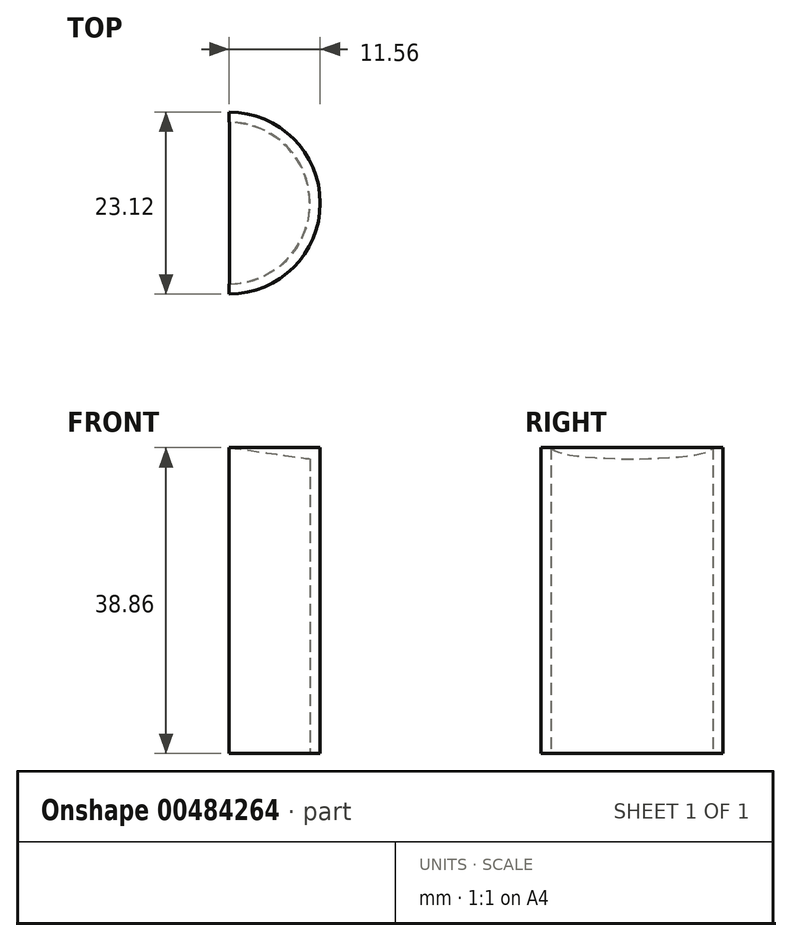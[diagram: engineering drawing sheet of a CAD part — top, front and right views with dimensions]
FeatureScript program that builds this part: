
annotation { "Feature Type Name" : "Feature", "Feature Type Description" : "" }
export const myFeature = defineFeature(function(context is Context, id is Id, definition is map)
    precondition{}
    {
        {
            var Q0;
            Q0=qCreatedBy(makeId("Top.planeOp"),FACE);
            var sketch = newSketch(context, id + "F0", { "sketchPlane" : qUnion([Q0])});
            skArc(sketch, "E0", {"start": v(0, -10.29) * mm, "mid": v(10.29, 0) * mm, "end": v(0, 10.29) * mm});
            skArc(sketch, "E1", {"start": v(0, -11.56) * mm, "mid": v(11.56, 0) * mm, "end": v(0, 11.56) * mm});
            skLineSegment(sketch, "E2", {"start": v(0, 11.56) * mm, "end": v(0, 10.29) * mm});
            skLineSegment(sketch, "E3.trimOffspring", {"start": v(0, -10.29) * mm, "end": v(0, -11.56) * mm});
            skSolve(sketch);
        }
        {
            var Q0;
            Q0=qSketchRegion(id+"F0",true);
            extrude(context, id + "F1", {"entities" : qUnion([Q0]), "endBound" : BoundingType.SYMMETRIC, "depth" : 38.1 * mm});
        }
        {
            var Q0;
            Q0=makeQuery(id+"F1.opExtrude","CAP_FACE",FACE,{"disambiguationData":[OSD([sQuery(id+"F0.wireOp",EDGE,"E0"),sQuery(id+"F0.wireOp",EDGE,"E1"),sQuery(id+"F0.wireOp",EDGE,"E2"),sQuery(id+"F0.wireOp",EDGE,"E3.trimOffspring")])],"isStart":false});
            var sketch = newSketch(context, id + "F2", { "sketchPlane" : qUnion([Q0])});
            skArc(sketch, "E4", {"start": v(0, -11.56) * mm, "mid": v(11.56, 0) * mm, "end": v(0, 11.56) * mm});
            skLineSegment(sketch, "E5", {"start": v(0, 11.56) * mm, "end": v(0, -11.56) * mm});
            skSolve(sketch);
        }
        {
            var Q0;
            Q0=qSketchRegion(id+"F2",true);
            extrude(context, id + "F3", {"entities" : qUnion([Q0]), "operationType" : NewBodyOperationType.ADD, "endBound" : BoundingType.SYMMETRIC, "depth" : 1.52 * mm});
        }
        {
            var Q0;
            Q0=makeQuery(id+"F3.opExtrude","CAP_EDGE",EDGE,{"disambiguationData":[OSD([sQuery(id+"F2.wireOp",EDGE,"E5")])],"isStart":true});
            chamfer(context, id + "F4", {"entities" : qUnion([Q0]), "chamferType" : ChamferType.OFFSET_ANGLE, "width" : 1.52 * mm, "oppositeDirection" : false, "angle" : 82 * degree, "tangentPropagation" : true});
        }
    });
